SOLIDWORKS PART (.sldprt)
format: sldprt  version: not decoded by parser v0  size: 135,680 bytes
history: native  units: mm
features: sketch x4, extrude x2, cut_extrude x2, fillet x2, material x1 (+13 scaffold rows collapsed)
feature tree (24):
  scaffold x13  (default folders/planes/origin — collapsed)
  material  "Material <not specified>"
  sketch  "Sketch1"  dims[D1=~6.476259mm]
  extrude  "Boss-Extrude1"  Depth=8mm
  sketch  "Sketch2"  dims[D1=7.0mm]
  extrude  "Boss-Extrude2"  Depth=10mm
  sketch  "Sketch3"  dims[D1=8.0mm]
  cut_extrude  "Cut-Extrude1"  Depth=10mm
  fillet  "Fillet1"  Radius=1mm
  sketch  "Sketch6"  dims[D1=15.0mm]
  cut_extrude  "Cut-Extrude3"  Depth=4.5mm
  fillet  "Fillet2"  Radius=2mm
decode coverage: 10 of 10 modeling features carry decoded parameters
note: ~ marks probable driven/reference dimensions
note: suppression state not decoded; provenance and decode notes live in map.json
